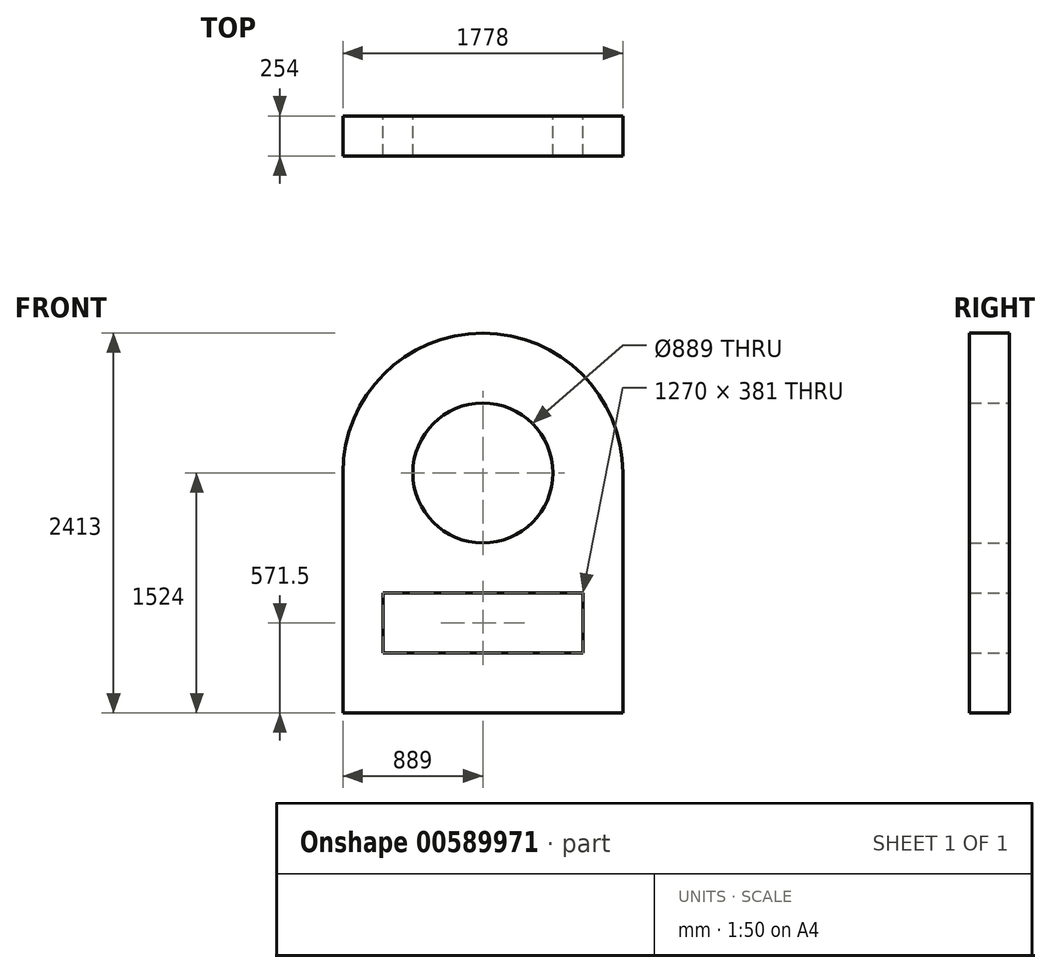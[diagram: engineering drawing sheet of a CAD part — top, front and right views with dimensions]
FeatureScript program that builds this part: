
annotation { "Feature Type Name" : "Feature", "Feature Type Description" : "" }
export const myFeature = defineFeature(function(context is Context, id is Id, definition is map)
    precondition{}
    {
        {
            var Q0;
            Q0=qCreatedBy(makeId("Front.planeOp"),FACE);
            var sketch = newSketch(context, id + "F0", { "sketchPlane" : qUnion([Q0])});
            skLineSegment(sketch, "E0", {"start": v(0, 0) * mm, "end": v(0, 1524) * mm});
            skLineSegment(sketch, "E1", {"start": v(0, 0) * mm, "end": v(1778, 0) * mm});
            skLineSegment(sketch, "E2", {"start": v(1778, 0) * mm, "end": v(1778, 1524) * mm});
            skLineSegment(sketch, "E3", {"start": v(254, 762) * mm, "end": v(254, 381) * mm});
            skLineSegment(sketch, "E4", {"start": v(254, 381) * mm, "end": v(1524, 381) * mm});
            skLineSegment(sketch, "E5", {"start": v(1524, 381) * mm, "end": v(1524, 762) * mm});
            skLineSegment(sketch, "E6", {"start": v(1524, 762) * mm, "end": v(254, 762) * mm});
            skPoint(sketch, "E7.centerSnap0", {"position": v(889, 762) * mm});
            skArc(sketch, "E8", {"start": v(1778, 1524) * mm, "mid": v(889, 2413) * mm, "end": v(0, 1524) * mm});
            skCircle(sketch, "E9", {"center": v(889, 1524) * mm, "radius": 444.5 * mm});
            skSolve(sketch);
        }
        {
            var Q0;
            Q0=makeQuery(id+"F0.imprint","IMPRINT",FACE,{"disambiguationData":[TD([[makeQuery(id+"F0.imprint","IMPRINT",EDGE,{"derivedFrom":sQuery(id+"F0.wireOp",EDGE,"E0")}),-1.0]])]});
            extrude(context, id + "F1", {"entities" : qUnion([Q0]), "depth" : 254 * mm, "offsetDistance" : 25.4 * mm});
        }
    });
